# Revit family: Sanitary_Taps-And-Mixers_Sanindusa_Eco-Concealed-Timer-Tap-For-Urinal
name_source: partatom
category: Plumbing Fixtures
revit_build: Autodesk Revit 2018 (Build: 20170223_1515(x64)
units: mm (PartAtom-declared; Revit-internal decimal feet)

## family parameters
Always vertical = Yes
Cut with Voids When Loaded = No
OmniClass Number = 23.45.00.00
OmniClass Title = Sanitary, Laundry, and Cleaning Equipment
Part Type = Normal
Room Calculation Point = No
Round Connector Dimension = Use Diameter
Shared = No
Work Plane-Based = No

## types (1)
- Sanitary_Taps-And-Mixers_Sanindusa_Eco-Concealed-Timer-Tap-For-Urinal
    AssetType = Fixed
    BodyMaterial = Brass
    CartridgeType = Timed cartridge
    Color = Silver
    Cost = 0 $
    Description = Concealed timer tap eco for urinal
    Edition number = 1
    Element Type = FAUCET: A small diameter valve, with a free outlet, from which water is drawn.
    FaucetFunction = Unset
    FaucetOperation = TimedSelfClosing
    FaucetTopDescription = Push button
    FaucetType = SprayMixing
    Features = Operates showers or urinals, compatible with thermostatic mixing valves, showerheads, arms and slide bar shower kits. With anti-water hammer system
    Finish = Chrome plated
    FlowCoefficient = Adjustable Flow: min 4l/min - máx 13l/min
    FlowRateMaximum = Adjustable Flow: min 4l/min - máx 13l/min
    InletConnectionType = G 1/2"
    Installation Instructions = https://www.tec.sanindusa.pt
    InstallationDate = 1900-12-31T23:59:59
    Manufacturer = Sanindusa
    ManufacturerName = Sanindusa
    ManufacturerURL = www.tec.sanindusa.pt
    Material = Brass
    ModelNumber = 5190541
    ModelReference = Eco
    Name = Eco concealed timer tap for urinal
    NominalHeight = 0 mm  [stored 0 ft]
    NominalLength = 0 mm  [stored 0 ft]
    NominalWidth = 0 mm  [stored 0 ft]
    OperatingMechanismMaterial = Brass
    OutletConnectionType = G 1/2"
    Pre-defined type (IFC) = FAUCET
    Product Guid = 19f8cbd6-4dad-4d88-a83f-a7dcdb0ac1e2
    Product data url = https://bimobject.com
    ProductInformation = https://www.tec.sanindusa.pt
    ProductionYear = 2018
    Shape = round
    Size = D118
    TestPressure = 0,5-6 bar
    Type (IFC) = IfcValveType
    URL = www.tec.sanindusa.pt
    Uniclass2015Version = Products v1.6
    ValveMechanism = OTHER
    ValveOperation = OTHER
    ValvePattern = UNSET
    Version = 1
    WarrantyDescription = https://www.tec.sanindusa.pt
    WarrantyDurationParts = 5
    WarrantyDurationUnit = year
    WarrantyStartDate = 1900-12-31T23:59:59
1900-12-31T23:59:59
    Weight = 0.70 kg
    WorkingPressure = 3 bar

note: [stored X ft] marks values corroborated as IEEE doubles in the binary element streams (Revit-internal decimal feet)

## geometry (parser evidence)
native form markers: Sweep x7
no freeform markers — native parametric forms only
